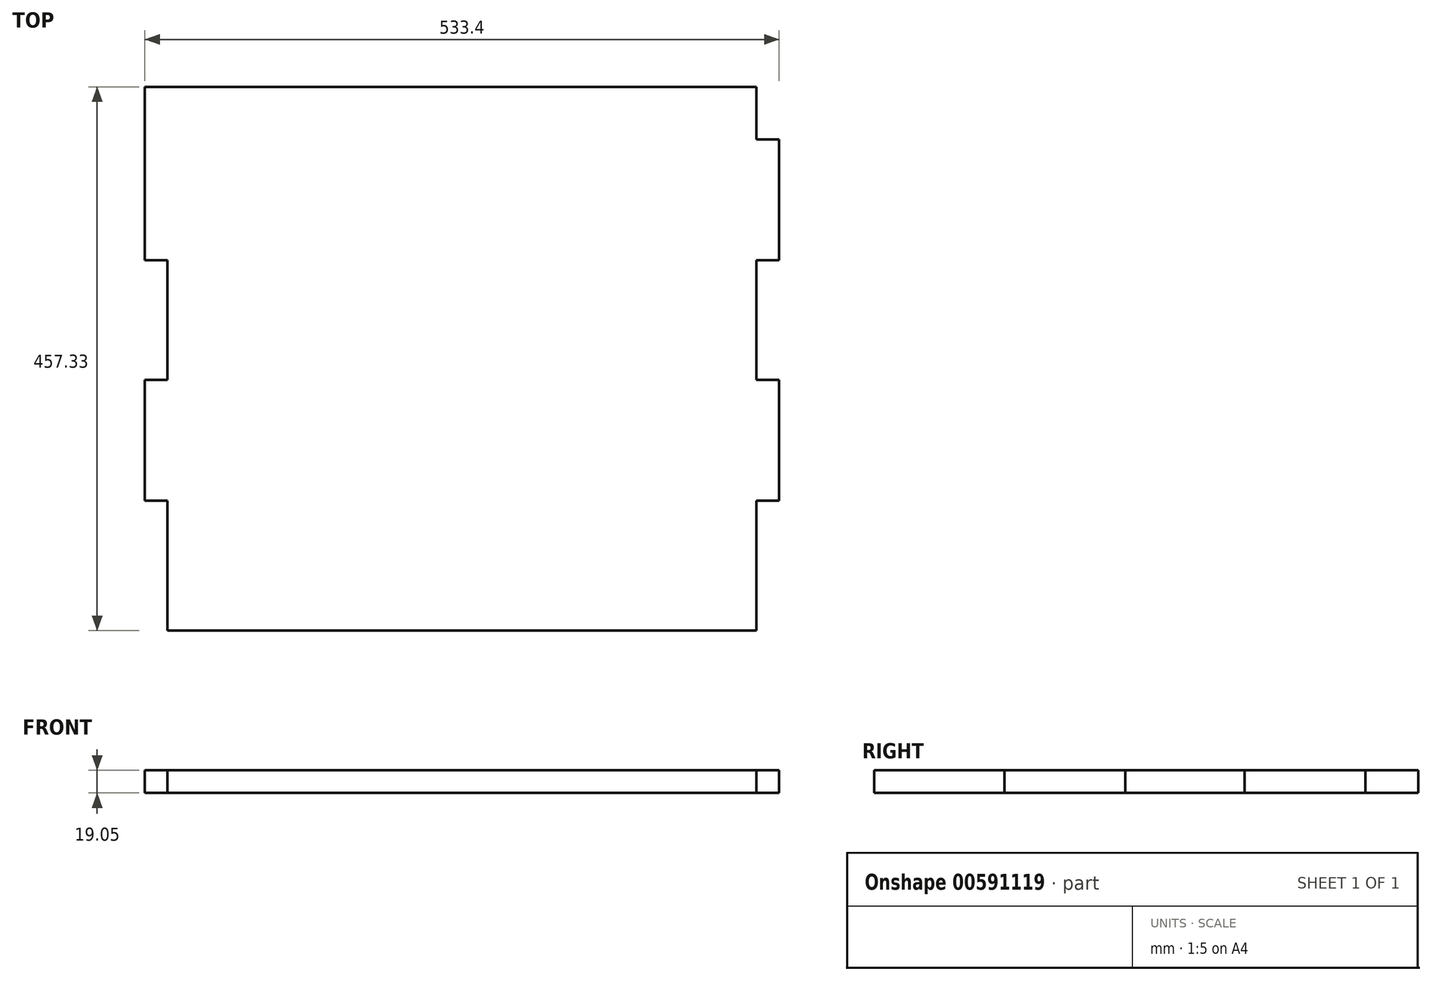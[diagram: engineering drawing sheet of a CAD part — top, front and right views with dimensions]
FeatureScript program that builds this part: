
annotation { "Feature Type Name" : "Feature", "Feature Type Description" : "" }
export const myFeature = defineFeature(function(context is Context, id is Id, definition is map)
    precondition{}
    {
        {
            var Q0;
            Q0=qCreatedBy(makeId("Top.planeOp"),FACE);
            var sketch = newSketch(context, id + "F0", { "sketchPlane" : qUnion([Q0])});
            skLineSegment(sketch, "E0.bottom", {"start": v(-480.8, -198.64) * mm, "end": v(52.6, -198.64) * mm});
            skLineSegment(sketch, "E0.top", {"start": v(-480.8, 258.7) * mm, "end": v(52.6, 258.7) * mm});
            skLineSegment(sketch, "E0.left", {"start": v(-480.8, -198.64) * mm, "end": v(-480.8, 258.7) * mm});
            skLineSegment(sketch, "E0.right", {"start": v(52.6, -198.64) * mm, "end": v(52.6, 258.7) * mm});
            skLineSegment(sketch, "E1", {"start": v(-480.8, 30.03) * mm, "end": v(52.6, 30.03) * mm, "construction": true});
            skLineSegment(sketch, "E2", {"start": v(-214.1, 258.7) * mm, "end": v(-214.1, -198.64) * mm, "construction": true});
            skLineSegment(sketch, "E3.left", {"start": v(-480.8, -89.21) * mm, "end": v(-480.8, 76.55) * mm});
            skLineSegment(sketch, "E4", {"start": v(-520.41, 258.7) * mm, "end": v(-520.41, 214.47) * mm, "construction": true});
            skLineSegment(sketch, "E5", {"start": v(-520.41, 214.47) * mm, "end": v(-520.41, 112.87) * mm, "construction": true});
            skLineSegment(sketch, "E6", {"start": v(-520.41, 112.87) * mm, "end": v(-520.41, 11.12) * mm, "construction": true});
            skLineSegment(sketch, "E7", {"start": v(-520.41, 11.12) * mm, "end": v(-520.41, -90.48) * mm, "construction": true});
            skLineSegment(sketch, "E8", {"start": v(-520.41, -198.64) * mm, "end": v(-520.41, -89.21) * mm, "construction": true});
            skLineSegment(sketch, "E9", {"start": v(-520.41, -89.21) * mm, "end": v(-520.41, 12.39) * mm, "construction": true});
            skLineSegment(sketch, "E10.bottom", {"start": v(-480.8, -89.21) * mm, "end": v(-461.74, -89.21) * mm});
            skLineSegment(sketch, "E10.top", {"start": v(-480.8, -198.64) * mm, "end": v(-461.74, -198.64) * mm});
            skLineSegment(sketch, "E10.left", {"start": v(-480.8, -89.21) * mm, "end": v(-480.8, -198.64) * mm});
            skLineSegment(sketch, "E10.right", {"start": v(-461.74, -89.21) * mm, "end": v(-461.74, -198.64) * mm});
            skLineSegment(sketch, "E11.left", {"start": v(-480.8, 11.12) * mm, "end": v(-480.8, 12.39) * mm});
            skLineSegment(sketch, "E11.right", {"start": v(-424.45, 11.12) * mm, "end": v(-424.45, 12.39) * mm});
            skLineSegment(sketch, "E12.bottom", {"start": v(-480.8, 12.39) * mm, "end": v(-461.74, 12.39) * mm});
            skLineSegment(sketch, "E12.top", {"start": v(-480.8, 112.87) * mm, "end": v(-461.74, 112.87) * mm});
            skLineSegment(sketch, "E12.left", {"start": v(-480.8, 12.39) * mm, "end": v(-480.8, 112.87) * mm});
            skLineSegment(sketch, "E12.right", {"start": v(-461.74, 12.39) * mm, "end": v(-461.74, 112.87) * mm});
            skLineSegment(sketch, "E13.bottom", {"start": v(-480.8, 258.7) * mm, "end": v(-461.74, 258.7) * mm});
            skLineSegment(sketch, "E13.top", {"start": v(-480.8, 214.47) * mm, "end": v(-461.74, 214.47) * mm});
            skLineSegment(sketch, "E13.left", {"start": v(-480.8, 258.7) * mm, "end": v(-480.8, 214.47) * mm});
            skLineSegment(sketch, "E13.right", {"start": v(-461.74, 258.7) * mm, "end": v(-461.74, 214.47) * mm});
            skLineSegment(sketch, "E14.MirrorCS", {"start": v(33.56, 12.39) * mm, "end": v(33.56, 112.87) * mm});
            skLineSegment(sketch, "E15.MirrorCS", {"start": v(33.56, -89.21) * mm, "end": v(33.56, -198.64) * mm});
            skLineSegment(sketch, "E16.MirrorCS", {"start": v(33.56, 258.7) * mm, "end": v(33.56, 214.47) * mm});
            skLineSegment(sketch, "E17.MirrorCS", {"start": v(52.6, 214.47) * mm, "end": v(33.56, 214.47) * mm});
            skLineSegment(sketch, "E18.MirrorCS", {"start": v(52.6, 12.39) * mm, "end": v(33.56, 12.39) * mm});
            skLineSegment(sketch, "E19.MirrorCS", {"start": v(52.6, 112.87) * mm, "end": v(33.56, 112.87) * mm});
            skLineSegment(sketch, "E20.MirrorCS", {"start": v(52.6, -198.64) * mm, "end": v(-480.8, -198.64) * mm});
            skLineSegment(sketch, "E21.MirrorCS", {"start": v(52.6, -89.21) * mm, "end": v(33.56, -89.21) * mm});
            skSolve(sketch);
        }
        {
            var Q0;
            Q0 = qSketchRegion(id + "F0", true);
            extrude(context, id + "F1", {"entities" : qUnion([Q0]), "depth" : 19.05 * mm, "offsetDistance" : 25.4 * mm});
        }
        {
            var Q0;
            {var subQ0=sQuery(id+"F0.wireOp",EDGE,"E12.bottom");Q0=makeQuery(id+"F0.imprint","IMPRINT",FACE,{"disambiguationData":[TD([[makeQuery(id+"F0.imprint","IMPRINT",EDGE,{"derivedFrom":subQ0}),1.0]])]});}
            var Q1;
            Q1=makeQuery(id+"F0.imprint","IMPRINT",FACE,{"disambiguationData":[TD([[makeQuery(id+"F0.imprint","IMPRINT",EDGE,{"derivedFrom":sQuery(id+"F0.wireOp",EDGE,"E13.bottom")}),-1.0]])]});
            var Q2;
            Q2=makeQuery(id+"F0.imprint","IMPRINT",FACE,{"disambiguationData":[TD([[makeQuery(id+"F0.imprint","IMPRINT",EDGE,{"derivedFrom":sQuery(id+"F0.wireOp",EDGE,"E10.bottom")}),-1.0]])]});
            var Q3;
            {var subQ4=sQuery(id+"F0.wireOp",EDGE,"E15.MirrorCS");Q3=makeQuery(id+"F0.imprint","IMPRINT",FACE,{"disambiguationData":[TD([[makeQuery(id+"F0.imprint","IMPRINT",EDGE,{"derivedFrom":subQ4}),1.0]])]});}
            var Q4;
            Q4=makeQuery(id+"F0.imprint","IMPRINT",FACE,{"disambiguationData":[TD([[makeQuery(id+"F0.imprint","IMPRINT",EDGE,{"derivedFrom":sQuery(id+"F0.wireOp",EDGE,"E14.MirrorCS")}),-1.0]])]});
            var Q5;
            {var subQ3=sQuery(id+"F0.wireOp",EDGE,"E16.MirrorCS");Q5=makeQuery(id+"F0.imprint","IMPRINT",FACE,{"disambiguationData":[TD([[makeQuery(id+"F0.imprint","IMPRINT",EDGE,{"derivedFrom":subQ3}),1.0]])]});}
            extrude(context, id + "F2", {"entities" : qUnion([Q0, Q1, Q2, Q3, Q4, Q5]), "operationType" : NewBodyOperationType.REMOVE, "endBound" : BoundingType.THROUGH_ALL, "depth" : 25.4 * mm, "offsetDistance" : 25.4 * mm});
        }
    });
